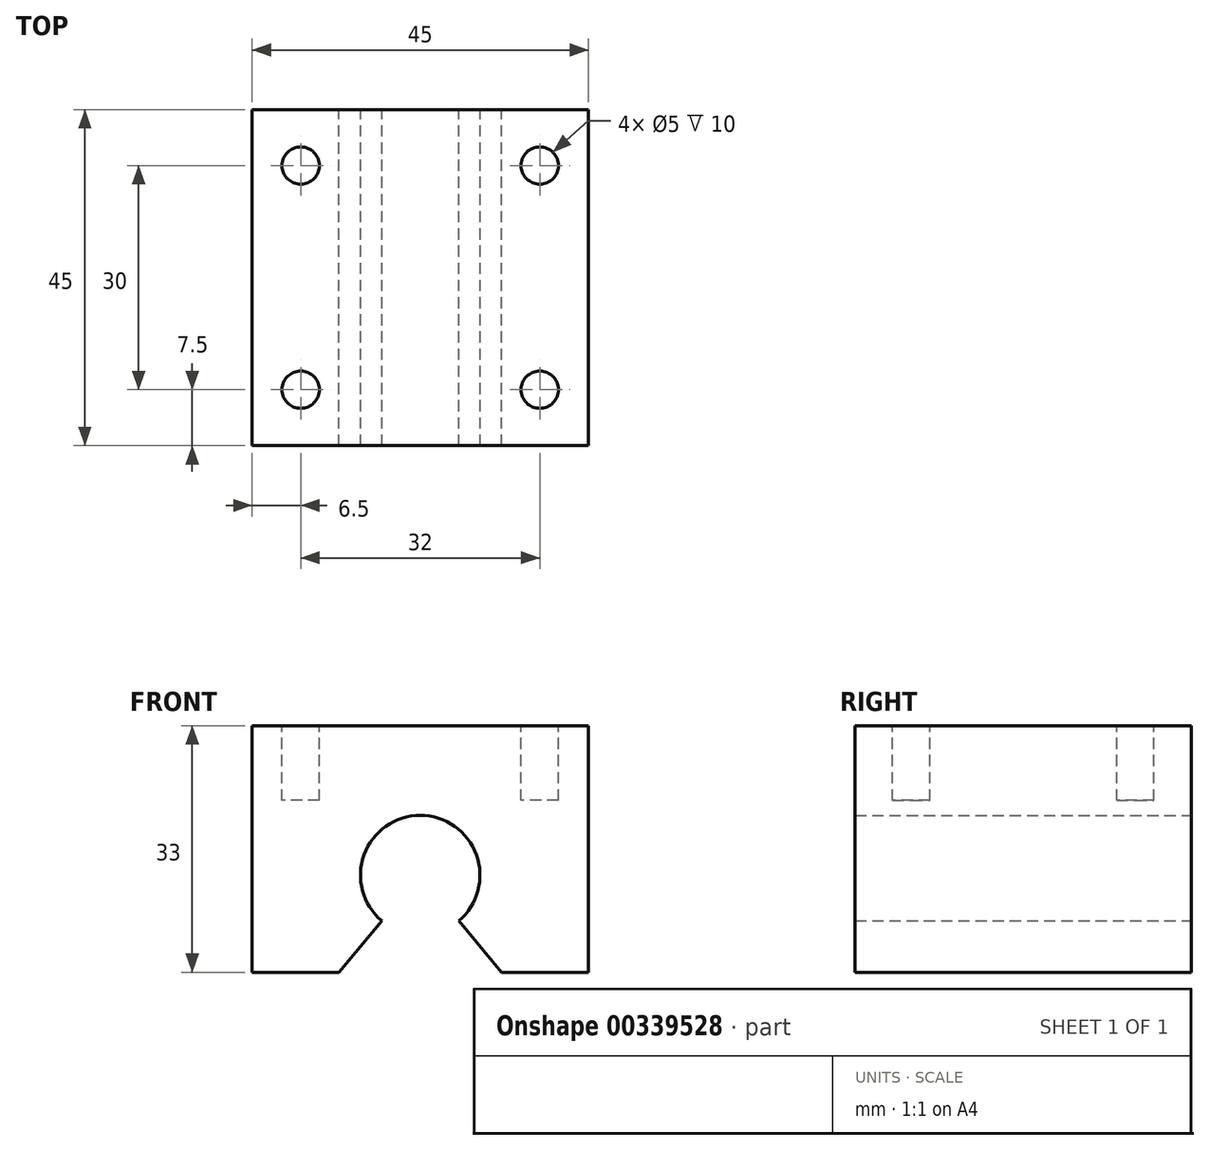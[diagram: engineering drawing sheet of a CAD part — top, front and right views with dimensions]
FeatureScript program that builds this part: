
annotation { "Feature Type Name" : "Feature", "Feature Type Description" : "" }
export const myFeature = defineFeature(function(context is Context, id is Id, definition is map)
    precondition{}
    {
        {
            var Q0;
            Q0=qCreatedBy(makeId("Front.planeOp"),FACE);
            var sketch = newSketch(context, id + "F0", { "sketchPlane" : qUnion([Q0])});
            skLineSegment(sketch, "E0.bottom", {"start": v(-24.53, 24.16) * mm, "end": v(20.47, 24.16) * mm});
            skLineSegment(sketch, "E0.top", {"start": v(-24.53, -8.84) * mm, "end": v(20.47, -8.84) * mm});
            skLineSegment(sketch, "E0.left", {"start": v(-24.53, 24.16) * mm, "end": v(-24.53, -8.84) * mm});
            skLineSegment(sketch, "E0.right", {"start": v(20.47, 24.16) * mm, "end": v(20.47, -8.84) * mm});
            skLineSegment(sketch, "E1", {"start": v(-2.03, 24.16) * mm, "end": v(-2.03, -8.84) * mm, "construction": true});
            skCircle(sketch, "E2", {"center": v(-2.03, 4.16) * mm, "radius": 8 * mm});
            skLineSegment(sketch, "E3", {"start": v(-2.03, 4.16) * mm, "end": v(-12.94, -8.84) * mm});
            skLineSegment(sketch, "E4", {"start": v(-2.03, 4.16) * mm, "end": v(8.88, -8.84) * mm});
            skSolve(sketch);
        }
        {
            var Q0;
            Q0=makeQuery(id+"F0.imprint","IMPRINT",FACE,{"disambiguationData":[TD([[makeQuery(id+"F0.imprint","IMPRINT",EDGE,{"derivedFrom":sQuery(id+"F0.wireOp",EDGE,"E0.bottom")}),-1.0]])]});
            extrude(context, id + "F1", {"entities" : qUnion([Q0]), "depth" : 45 * mm});
        }
        {
            var Q0;
            Q0=makeQuery(id+"F1.opExtrude","SWEPT_FACE",FACE,{"disambiguationData":[OSD([sQuery(id+"F0.wireOp",EDGE,"E0.bottom")])]});
            var sketch = newSketch(context, id + "F2", { "sketchPlane" : qUnion([Q0])});
            skLineSegment(sketch, "E5", {"start": v(-24.53, -7.5) * mm, "end": v(20.47, -7.5) * mm, "construction": true});
            skLineSegment(sketch, "E6", {"start": v(-24.53, -37.5) * mm, "end": v(20.47, -37.5) * mm, "construction": true});
            skLineSegment(sketch, "E7", {"start": v(-18.03, 0) * mm, "end": v(-18.03, -45) * mm, "construction": true});
            skLineSegment(sketch, "E8", {"start": v(13.97, 0) * mm, "end": v(13.97, -45) * mm, "construction": true});
            skCircle(sketch, "E9", {"center": v(-18.03, -7.5) * mm, "radius": 2.5 * mm});
            skCircle(sketch, "E10", {"center": v(13.97, -7.5) * mm, "radius": 2.5 * mm});
            skCircle(sketch, "E11", {"center": v(-18.03, -37.5) * mm, "radius": 2.5 * mm});
            skCircle(sketch, "E12", {"center": v(13.97, -37.5) * mm, "radius": 2.5 * mm});
            skSolve(sketch);
        }
        {
            var Q0;
            Q0=makeQuery(id+"F2.imprint","IMPRINT",FACE,{"disambiguationData":[TD([[makeQuery(id+"F2.imprint","IMPRINT",EDGE,{"derivedFrom":sQuery(id+"F2.wireOp",EDGE,"E10")}),1.0]])]});
            var Q1;
            Q1=makeQuery(id+"F2.imprint","IMPRINT",FACE,{"disambiguationData":[TD([[makeQuery(id+"F2.imprint","IMPRINT",EDGE,{"derivedFrom":sQuery(id+"F2.wireOp",EDGE,"E11")}),1.0]])]});
            var Q2;
            Q2=makeQuery(id+"F2.imprint","IMPRINT",FACE,{"disambiguationData":[TD([[makeQuery(id+"F2.imprint","IMPRINT",EDGE,{"derivedFrom":sQuery(id+"F2.wireOp",EDGE,"E12")}),1.0]])]});
            var Q3;
            Q3=makeQuery(id+"F2.imprint","IMPRINT",FACE,{"disambiguationData":[TD([[makeQuery(id+"F2.imprint","IMPRINT",EDGE,{"derivedFrom":sQuery(id+"F2.wireOp",EDGE,"E9")}),1.0]])]});
            extrude(context, id + "F3", {"entities" : qUnion([Q0, Q1, Q2, Q3]), "operationType" : NewBodyOperationType.REMOVE, "oppositeDirection" : true, "depth" : 10 * mm});
        }
    });
